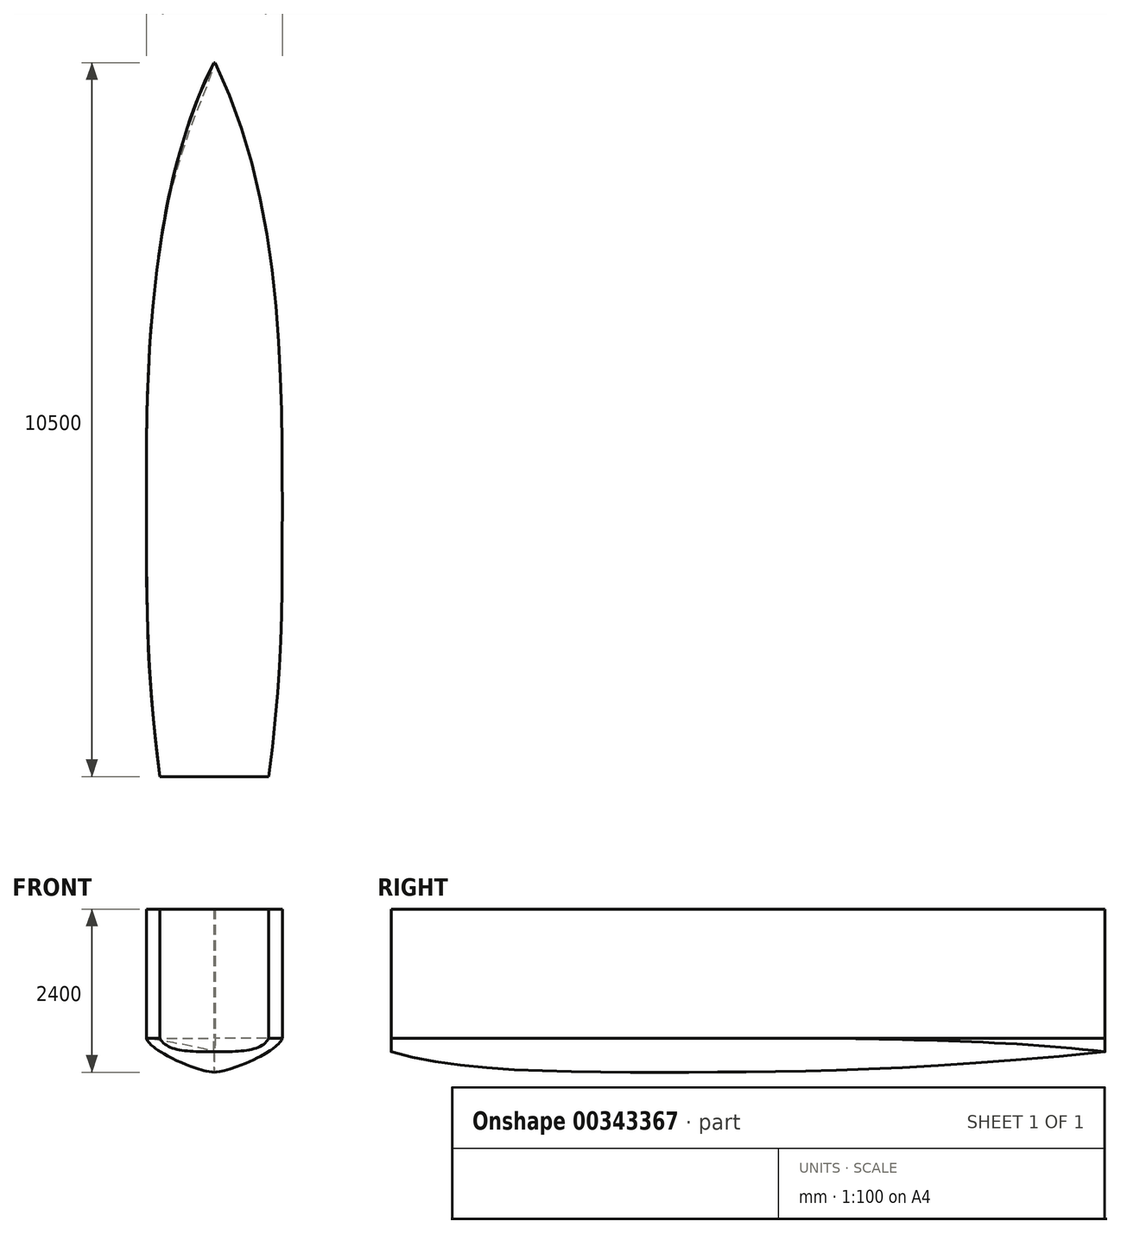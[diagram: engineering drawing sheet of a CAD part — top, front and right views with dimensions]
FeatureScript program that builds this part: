
annotation { "Feature Type Name" : "Feature", "Feature Type Description" : "" }
export const myFeature = defineFeature(function(context is Context, id is Id, definition is map)
    precondition{}
    {
        {
            var Q0;
            Q0=qCreatedBy(makeId("Right.planeOp"),FACE);
            var sketch = newSketch(context, id + "F0", { "sketchPlane" : qUnion([Q0])});
            skLineSegment(sketch, "E0.bottom", {"start": v(0, 0) * mm, "end": v(10500, 0) * mm});
            skLineSegment(sketch, "E0.top", {"start": v(0, 2400) * mm, "end": v(10500, 2400) * mm});
            skLineSegment(sketch, "E0.left", {"start": v(0, 0) * mm, "end": v(0, 2400) * mm});
            skLineSegment(sketch, "E0.right", {"start": v(10500, 0) * mm, "end": v(10500, 2400) * mm});
            skLineSegment(sketch, "E1", {"start": v(0, 300) * mm, "end": v(10500, 300) * mm});
            skPoint(sketch, "E2", {"position": v(4000, 0) * mm});
            skFitSpline(sketch, "E3", {"points": [v(0, 300) * mm, v(4000, 0) * mm, v(10500, 300) * mm], "startDerivative": vector(6820.94, -2046.28) * mm, "endDerivative": vector(16066.33, 1606.63) * mm});
            skLineSegment(sketch, "E4", {"start": v(4000, 0) * mm, "end": v(4000, 2400) * mm});
            skPoint(sketch, "E5", {"position": v(4000, 300) * mm});
            skSolve(sketch);
        }
        {
            var Q0;
            Q0=qCreatedBy(makeId("Top.planeOp"),FACE);
            var Q1;
            Q1=sQuery(id+"F0.wireOp",VERTEX,"E0.left.end");
            cPlane(context, id + "F1", {"entities" : qUnion([Q0, Q1]), "cplaneType" : CPlaneType.PLANE_POINT, "offset" : 25 * mm, "width" : 150 * mm, "height" : 150 * mm});
        }
        {
            var Q0;
            Q0=qCreatedBy(makeId("Front.planeOp"),FACE);
            var sketch = newSketch(context, id + "F2", { "sketchPlane" : qUnion([Q0])});
            skLineSegment(sketch, "E6.bottom", {"start": v(0, 300) * mm, "end": v(800, 300) * mm});
            skLineSegment(sketch, "E6.top", {"start": v(0, 2400) * mm, "end": v(800, 2400) * mm});
            skLineSegment(sketch, "E6.left", {"start": v(0, 300) * mm, "end": v(0, 2400) * mm});
            skLineSegment(sketch, "E6.right", {"start": v(800, 300) * mm, "end": v(800, 2400) * mm});
            skLineSegment(sketch, "E7.MirrorCS", {"start": v(-800, 300) * mm, "end": v(-800, 2400) * mm});
            skLineSegment(sketch, "E8", {"start": v(-800, 2400) * mm, "end": v(0, 2400) * mm});
            skLineSegment(sketch, "E9", {"start": v(-800, 300) * mm, "end": v(0, 300) * mm});
            skLineSegment(sketch, "E10", {"start": v(-800, 500) * mm, "end": v(800, 500) * mm});
            skPoint(sketch, "E11", {"position": v(0, 500) * mm});
            skFitSpline(sketch, "E12", {"points": [v(-800, 500) * mm, v(0, 300) * mm, v(800, 500) * mm], "startDerivative": vector(600, -1200) * mm, "endDerivative": vector(600, 1200) * mm});
            skSolve(sketch);
        }
        {
            var Q0;
            Q0=qCreatedBy(id+"F1.planeOp",FACE);
            var sketch = newSketch(context, id + "F3", { "sketchPlane" : qUnion([Q0])});
            skLineSegment(sketch, "E13.bottom", {"start": v(0, 0) * mm, "end": v(1000, 0) * mm});
            skLineSegment(sketch, "E13.top", {"start": v(0, 10500) * mm, "end": v(1000, 10500) * mm});
            skLineSegment(sketch, "E13.left", {"start": v(0, 0) * mm, "end": v(0, 10500) * mm});
            skLineSegment(sketch, "E13.right", {"start": v(1000, 0) * mm, "end": v(1000, 10500) * mm});
            skLineSegment(sketch, "E14.MirrorCS", {"start": v(-1000, 0) * mm, "end": v(-1000, 10500) * mm});
            skLineSegment(sketch, "E15", {"start": v(-1000, 0) * mm, "end": v(0, 0) * mm});
            skLineSegment(sketch, "E16", {"start": v(-1000, 10500) * mm, "end": v(0, 10500) * mm});
            skLineSegment(sketch, "E17", {"start": v(0, 4000) * mm, "end": v(1000, 4000) * mm});
            skLineSegment(sketch, "E18.MirrorCS", {"start": v(0, 4000) * mm, "end": v(-1000, 4000) * mm});
            skPoint(sketch, "E19", {"position": v(800, 0) * mm});
            skPoint(sketch, "E20.MirrorP", {"position": v(-800, 0) * mm});
            skLineSegment(sketch, "E21", {"start": v(1000, 1500) * mm, "end": v(-1000, 1500) * mm});
            skPoint(sketch, "E22", {"position": v(10, 10500) * mm});
            skPoint(sketch, "E23.MirrorP", {"position": v(-10, 10500) * mm});
            skFitSpline(sketch, "E24", {"points": [v(800, 0) * mm, v(1000, 4000) * mm, v(10, 10500) * mm], "startDerivative": vector(1368.77, 10265.78) * mm, "endDerivative": vector(-5287.99, 10682.8) * mm});
            skLineSegment(sketch, "E25", {"start": v(-1000, 8500) * mm, "end": v(1000, 8500) * mm});
            skFitSpline(sketch, "E26", {"points": [v(-800, 0) * mm, v(-1000, 4000) * mm, v(-10, 10500) * mm], "startDerivative": vector(-1368.77, 10265.78) * mm, "endDerivative": vector(5287.99, 10682.8) * mm});
            skSolve(sketch);
        }
        {
            var Q0;
            Q0=qCreatedBy(makeId("Top.planeOp"),FACE);
            var Q1;
            Q1=sQuery(id+"F2.wireOp",VERTEX,"E11");
            cPlane(context, id + "F4", {"entities" : qUnion([Q0, Q1]), "cplaneType" : CPlaneType.PLANE_POINT, "offset" : 25 * mm, "width" : 150 * mm, "height" : 150 * mm});
        }
        {
            var Q0;
            Q0=qCreatedBy(makeId("Front.planeOp"),FACE);
            var Q1;
            Q1=sQuery(id+"F0.wireOp",VERTEX,"E3.2.internal");
            cPlane(context, id + "F5", {"entities" : qUnion([Q0, Q1]), "cplaneType" : CPlaneType.PLANE_POINT, "offset" : 25 * mm, "width" : 150 * mm, "height" : 150 * mm});
        }
        {
            var Q0;
            Q0=qCreatedBy(id+"F4.planeOp",FACE);
            var sketch = newSketch(context, id + "F6", { "sketchPlane" : qUnion([Q0])});
            skLineSegment(sketch, "E27.bottom", {"start": v(0, 0) * mm, "end": v(1000, 0) * mm});
            skLineSegment(sketch, "E27.top", {"start": v(0, 10500) * mm, "end": v(1000, 10500) * mm});
            skLineSegment(sketch, "E27.left", {"start": v(0, 0) * mm, "end": v(0, 10500) * mm});
            skLineSegment(sketch, "E27.right", {"start": v(1000, 0) * mm, "end": v(1000, 10500) * mm});
            skPoint(sketch, "E28", {"position": v(0, 4000) * mm});
            skLineSegment(sketch, "E29", {"start": v(0, 4000) * mm, "end": v(1000, 4000) * mm});
            skLineSegment(sketch, "E30.MirrorCS", {"start": v(0, 4000) * mm, "end": v(-1000, 4000) * mm});
            skLineSegment(sketch, "E31.MirrorCS", {"start": v(-1000, 0) * mm, "end": v(-1000, 10500) * mm});
            skLineSegment(sketch, "E32", {"start": v(-1000, 0) * mm, "end": v(0, 0) * mm});
            skLineSegment(sketch, "E33", {"start": v(-1000, 10500) * mm, "end": v(0, 10500) * mm});
            skPoint(sketch, "E34", {"position": v(800, 0) * mm});
            skPoint(sketch, "E35.MirrorP", {"position": v(-800, 0) * mm});
            skLineSegment(sketch, "E36", {"start": v(-1000, 1500) * mm, "end": v(1000, 1500) * mm});
            skPoint(sketch, "E37", {"position": v(10, 10500) * mm});
            skPoint(sketch, "E38.MirrorP", {"position": v(-10, 10500) * mm});
            skFitSpline(sketch, "E39", {"points": [v(800, 0) * mm, v(1000, 4000) * mm, v(10, 10500) * mm], "startDerivative": vector(1368.77, 10265.78) * mm, "endDerivative": vector(-5287.99, 10682.8) * mm});
            skLineSegment(sketch, "E40", {"start": v(-1000, 8500) * mm, "end": v(1000, 8500) * mm});
            skFitSpline(sketch, "E41", {"points": [v(-800, 0) * mm, v(-1000, 4000) * mm, v(-10, 10500) * mm], "startDerivative": vector(-1368.77, 10265.78) * mm, "endDerivative": vector(5287.99, 10682.8) * mm});
            skSolve(sketch);
        }
        {
            var Q0;
            Q0=qCreatedBy(id+"F5.planeOp",FACE);
            var sketch = newSketch(context, id + "F7", { "sketchPlane" : qUnion([Q0])});
            skLineSegment(sketch, "E42.bottom", {"start": v(0, 2400) * mm, "end": v(-10, 2400) * mm});
            skLineSegment(sketch, "E42.top", {"start": v(0, 300) * mm, "end": v(-10, 300) * mm});
            skLineSegment(sketch, "E42.left", {"start": v(0, 2400) * mm, "end": v(0, 300) * mm});
            skLineSegment(sketch, "E42.right", {"start": v(-10, 2400) * mm, "end": v(-10, 300) * mm});
            skLineSegment(sketch, "E43.MirrorCS", {"start": v(10, 2400) * mm, "end": v(10, 300) * mm});
            skLineSegment(sketch, "E44", {"start": v(0, 2400) * mm, "end": v(10, 2400) * mm});
            skLineSegment(sketch, "E45", {"start": v(0, 300) * mm, "end": v(10, 300) * mm});
            skPoint(sketch, "E46", {"position": v(0, 500) * mm});
            skLineSegment(sketch, "E47", {"start": v(0, 500) * mm, "end": v(10, 500) * mm});
            skLineSegment(sketch, "E48", {"start": v(0, 500) * mm, "end": v(-10, 500) * mm});
            skFitSpline(sketch, "E49", {"points": [v(10, 500) * mm, v(0, 300) * mm, v(-10, 500) * mm], "startDerivative": vector(0, -1200) * mm, "endDerivative": vector(0, 1200) * mm});
            skSolve(sketch);
        }
        {
            var Q0;
            {var subQ0=sQuery(id+"F2.wireOp",EDGE,"E6.top");Q0=makeQuery(id+"F2.imprint","IMPRINT",FACE,{"disambiguationData":[TD([[makeQuery(id+"F2.imprint","IMPRINT",EDGE,{"derivedFrom":subQ0}),-1.0]])]});}
            var Q1;
            {var subQ0=sQuery(id+"F7.wireOp",EDGE,"E44");Q1=makeQuery(id+"F7.imprint","IMPRINT",FACE,{"disambiguationData":[TD([[makeQuery(id+"F7.imprint","IMPRINT",EDGE,{"derivedFrom":subQ0}),-1.0]])]});}
            var Q2;
            Q2=sQuery(id+"F3.wireOp",EDGE,"E24");
            var Q3;
            Q3=sQuery(id+"F6.wireOp",EDGE,"E39");
            loft(context, id + "F8", {"addGuides" : true, "sheetProfilesArray" : [{ "sheetProfileEntities" : qUnion([Q0]) }, { "sheetProfileEntities" : qUnion([Q1]) }], "guidesArray" : [{ "guideEntities" : qUnion([Q2]), "guideDerivativeType" : LoftGuideDerivativeType.DEFAULT, "guideDerivativeMagnitude" : 1 }, { "guideEntities" : qUnion([Q3]), "guideDerivativeType" : LoftGuideDerivativeType.DEFAULT, "guideDerivativeMagnitude" : 1 }]});
        }
        {
            var Q1;
            {var subQ1=sQuery(id+"F2.wireOp",EDGE,"E6.left");var subQ3=sQuery(id+"F2.wireOp",EDGE,"E10");var subQ4=makeQuery(id+"F2.imprint","INTERSECT",VERTEX,{"derivedFrom":[subQ1,subQ3]});Q1=makeQuery(id+"F2.imprint","IMPRINT",FACE,{"disambiguationData":[TD([[makeQuery(id+"F2.imprint","IMPRINT",EDGE,{"disambiguationData":[TD([[subQ4,-1.0]])],"derivedFrom":subQ3}),-1.0]])]});}
            var Q2;
            {var subQ3=sQuery(id+"F7.wireOp",EDGE,"E47");Q2=makeQuery(id+"F7.imprint","IMPRINT",FACE,{"disambiguationData":[TD([[makeQuery(id+"F7.imprint","IMPRINT",EDGE,{"derivedFrom":subQ3}),-1.0]])]});}
            var Q3;
            Q3=makeQuery(id+"F8.opLoft","SWEPT_EDGE",EDGE,{"disambiguationData":[OSD([sQuery(id+"F6.wireOp",EDGE,"E39")])]});
            var Q4;
            Q4=sQuery(id+"F0.wireOp",EDGE,"E3");
            loft(context, id + "F9", {"operationType" : NewBodyOperationType.ADD, "addGuides" : true, "sheetProfilesArray" : [{ "sheetProfileEntities" : qUnion([Q1]) }, { "sheetProfileEntities" : qUnion([Q2]) }], "guidesArray" : [{ "guideEntities" : qUnion([Q3]), "guideDerivativeType" : LoftGuideDerivativeType.DEFAULT, "guideDerivativeMagnitude" : 1 }, { "guideEntities" : qUnion([Q4]), "guideDerivativeType" : LoftGuideDerivativeType.DEFAULT, "guideDerivativeMagnitude" : 1 }]});
        }
        {
            var Q1;
            {var subQ0=sQuery(id+"F2.wireOp",EDGE,"E8");Q1=makeQuery(id+"F2.imprint","IMPRINT",FACE,{"disambiguationData":[TD([[makeQuery(id+"F2.imprint","IMPRINT",EDGE,{"derivedFrom":subQ0}),-1.0]])]});}
            var Q2;
            {var subQ0=sQuery(id+"F7.wireOp",EDGE,"E42.bottom");Q2=makeQuery(id+"F7.imprint","IMPRINT",FACE,{"disambiguationData":[TD([[makeQuery(id+"F7.imprint","IMPRINT",EDGE,{"derivedFrom":subQ0}),1.0]])]});}
            var Q3;
            Q3=sQuery(id+"F6.wireOp",EDGE,"E41");
            var Q4;
            Q4=sQuery(id+"F3.wireOp",EDGE,"E26");
            loft(context, id + "F10", {"operationType" : NewBodyOperationType.ADD, "addGuides" : true, "sheetProfilesArray" : [{ "sheetProfileEntities" : qUnion([Q1]) }, { "sheetProfileEntities" : qUnion([Q2]) }], "guidesArray" : [{ "guideEntities" : qUnion([Q3]), "guideDerivativeType" : LoftGuideDerivativeType.DEFAULT, "guideDerivativeMagnitude" : 1 }, { "guideEntities" : qUnion([Q4]), "guideDerivativeType" : LoftGuideDerivativeType.DEFAULT, "guideDerivativeMagnitude" : 1 }]});
        }
        {
            var Q1;
            {var subQ1=sQuery(id+"F2.wireOp",EDGE,"E6.left");var subQ3=sQuery(id+"F2.wireOp",EDGE,"E10");var subQ4=makeQuery(id+"F2.imprint","INTERSECT",VERTEX,{"derivedFrom":[subQ1,subQ3]});Q1=makeQuery(id+"F2.imprint","IMPRINT",FACE,{"disambiguationData":[TD([[makeQuery(id+"F2.imprint","IMPRINT",EDGE,{"disambiguationData":[TD([[subQ4,1.0]])],"derivedFrom":subQ3}),-1.0]])]});}
            var Q2;
            {var subQ3=sQuery(id+"F7.wireOp",EDGE,"E48");Q2=makeQuery(id+"F7.imprint","IMPRINT",FACE,{"disambiguationData":[TD([[makeQuery(id+"F7.imprint","IMPRINT",EDGE,{"derivedFrom":subQ3}),1.0]])]});}
            var Q3;
            Q3=sQuery(id+"F6.wireOp",EDGE,"E41");
            var Q4;
            Q4=makeQuery(id+"F9.opLoft","SWEPT_EDGE",EDGE,{"disambiguationData":[OSD([sQuery(id+"F0.wireOp",EDGE,"E3")])]});
            loft(context, id + "F11", {"operationType" : NewBodyOperationType.ADD, "addGuides" : true, "sheetProfilesArray" : [{ "sheetProfileEntities" : qUnion([Q1]) }, { "sheetProfileEntities" : qUnion([Q2]) }], "guidesArray" : [{ "guideEntities" : qUnion([Q3]), "guideDerivativeType" : LoftGuideDerivativeType.DEFAULT, "guideDerivativeMagnitude" : 1 }, { "guideEntities" : qUnion([Q4]), "guideDerivativeType" : LoftGuideDerivativeType.DEFAULT, "guideDerivativeMagnitude" : 1 }]});
        }
    });
